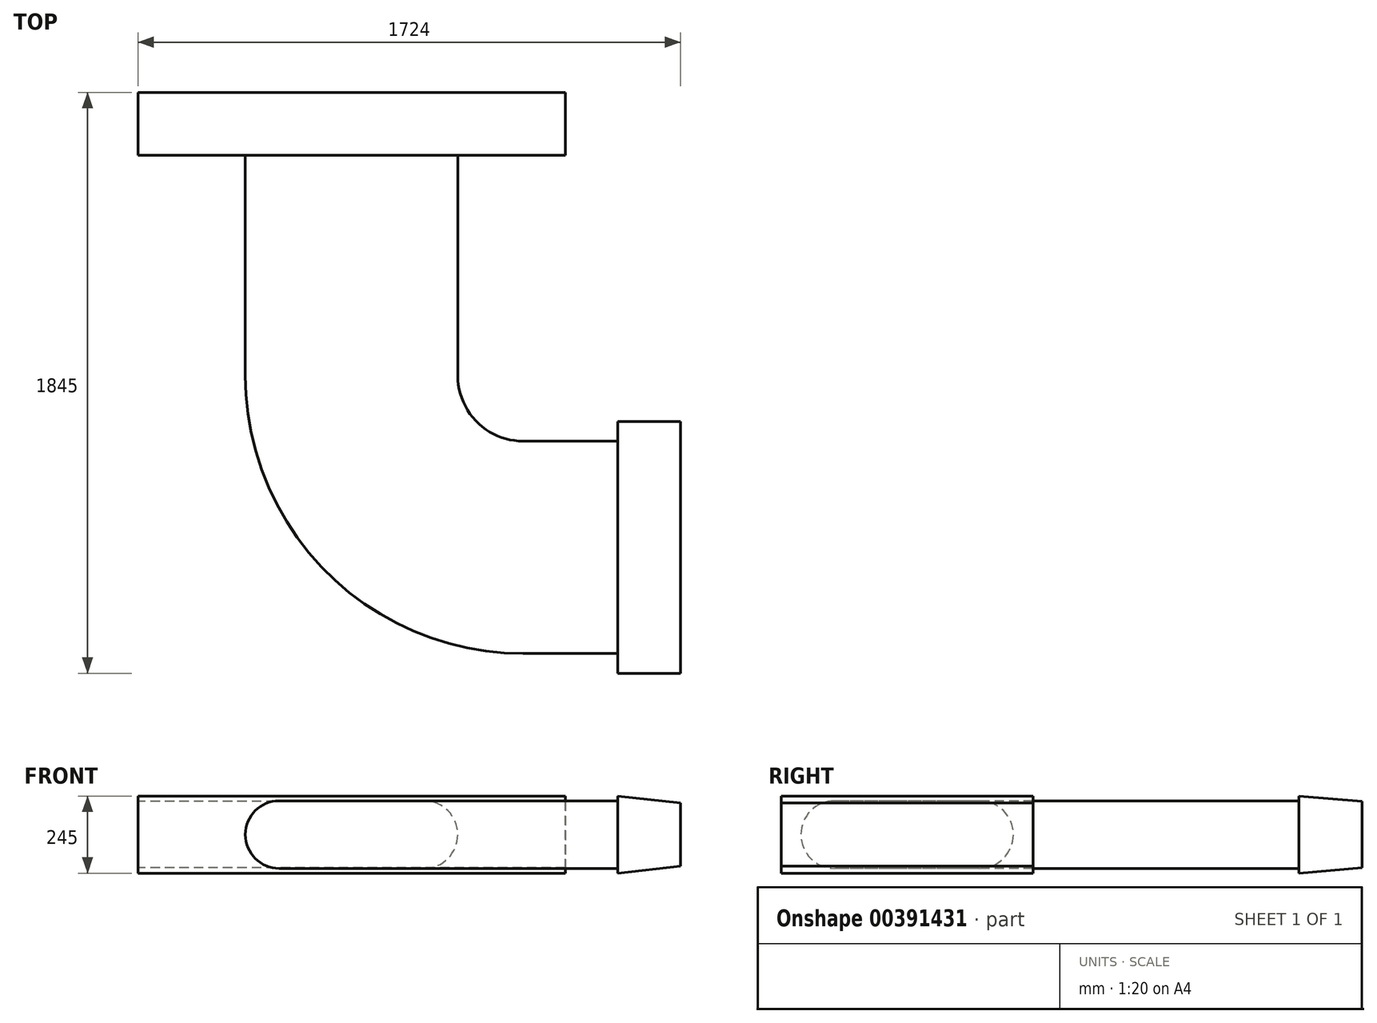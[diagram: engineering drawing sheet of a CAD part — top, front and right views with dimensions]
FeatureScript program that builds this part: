
annotation { "Feature Type Name" : "Feature", "Feature Type Description" : "" }
export const myFeature = defineFeature(function(context is Context, id is Id, definition is map)
    precondition{}
    {
        {
            var Q0;
            Q0=qCreatedBy(makeId("Right.planeOp"),FACE);
            var sketch = newSketch(context, id + "F0", { "sketchPlane" : qUnion([Q0])});
            skLineSegment(sketch, "E0", {"start": v(0, 0) * mm, "end": v(0, 105) * mm});
            skLineSegment(sketch, "E1", {"start": v(0, 0) * mm, "end": v(0, -105) * mm});
            skLineSegment(sketch, "E2", {"start": v(0, 105) * mm, "end": v(-200, 105) * mm, "construction": true});
            skLineSegment(sketch, "E3", {"start": v(0, -105) * mm, "end": v(-200, -105) * mm, "construction": true});
            skLineSegment(sketch, "E4", {"start": v(-200, 105) * mm, "end": v(-200, 122.5) * mm, "construction": true});
            skLineSegment(sketch, "E5", {"start": v(-200, -105) * mm, "end": v(-200, -122.5) * mm, "construction": true});
            skLineSegment(sketch, "E6", {"start": v(-200, 122.5) * mm, "end": v(0, 105) * mm});
            skLineSegment(sketch, "E7", {"start": v(0, -105) * mm, "end": v(-200, -122.5) * mm});
            skLineSegment(sketch, "E8", {"start": v(-200, -122.5) * mm, "end": v(-200, 122.5) * mm});
            skSolve(sketch);
        }
        {
            var Q0;
            Q0=makeQuery(id+"F0.imprint","IMPRINT",FACE,{"disambiguationData":[TD([[makeQuery(id+"F0.imprint","IMPRINT",EDGE,{"derivedFrom":sQuery(id+"F0.wireOp",EDGE,"E0")}),1.0]])]});
            extrude(context, id + "F1", {"entities" : qUnion([Q0]), "depth" : 679 * mm, "hasSecondDirection" : true, "secondDirectionOppositeDirection" : true, "secondDirectionDepth" : 679 * mm});
        }
        {
            var Q0;
            Q0=makeQuery(id+"F1.opExtrude","SWEPT_FACE",FACE,{"disambiguationData":[OSD([sQuery(id+"F0.wireOp",EDGE,"E8")])]});
            var sketch = newSketch(context, id + "F2", { "sketchPlane" : qUnion([Q0])});
            skPoint(sketch, "E9.0", {"position": v(0, 0) * mm});
            skLineSegment(sketch, "E10.bottom", {"start": v(230, -107.5) * mm, "end": v(-230, -107.5) * mm});
            skLineSegment(sketch, "E10.top", {"start": v(230, 107.5) * mm, "end": v(-230, 107.5) * mm});
            skArc(sketch, "E11", {"start": v(-230, 107.5) * mm, "mid": v(-337.5, 0) * mm, "end": v(-230, -107.5) * mm});
            skArc(sketch, "E12", {"start": v(230, -107.5) * mm, "mid": v(337.5, 0) * mm, "end": v(230, 107.5) * mm});
            skSolve(sketch);
        }
        {
            var Q0;
            Q0=makeQuery(id+"F2.imprint","IMPRINT",FACE,{"disambiguationData":[TD([[makeQuery(id+"F2.imprint","IMPRINT",EDGE,{"derivedFrom":sQuery(id+"F2.wireOp",EDGE,"E10.bottom")}),-1.0]])]});
            extrude(context, id + "F3", {"entities" : qUnion([Q0]), "operationType" : NewBodyOperationType.ADD, "depth" : 700 * mm});
        }
        {
            var Q0;
            Q0=makeQuery(id+"F3.opExtrude","CAP_FACE",FACE,{"disambiguationData":[OSD([sQuery(id+"F2.wireOp",EDGE,"E10.bottom"),sQuery(id+"F2.wireOp",EDGE,"E10.top"),sQuery(id+"F2.wireOp",EDGE,"E11"),sQuery(id+"F2.wireOp",EDGE,"E12")])],"isStart":false});
            var sketch = newSketch(context, id + "F4", { "sketchPlane" : qUnion([Q0])});
            skLineSegment(sketch, "E13", {"start": v(0, 107.5) * mm, "end": v(0, -107.5) * mm, "construction": true});
            skLineSegment(sketch, "E14", {"start": v(337.5, 0) * mm, "end": v(-337.5, 0) * mm, "construction": true});
            skPoint(sketch, "E15", {"position": v(0, 0) * mm});
            skSolve(sketch);
        }
        {
            var Q0;
            Q0=sQuery(id+"F4.wireOp",EDGE,"E14");
            cPlane(context, id + "F5", {"entities" : qUnion([Q0]), "cplaneType" : CPlaneType.LINE_ANGLE, "offset" : 25 * mm, "angle" : 90 * degree, "width" : 150 * mm, "height" : 150 * mm});
        }
        {
            var Q0;
            Q0=qCreatedBy(id+"F5.planeOp",FACE);
            var sketch = newSketch(context, id + "F6", { "sketchPlane" : qUnion([Q0])});
            skPoint(sketch, "E16.0", {"position": v(0, -900) * mm});
            skLineSegment(sketch, "E17", {"start": v(0, -900) * mm, "end": v(545, -900) * mm, "construction": true});
            skLineSegment(sketch, "E18", {"start": v(545, -900) * mm, "end": v(545, -1445) * mm, "construction": true});
            skArc(sketch, "E19", {"start": v(0, -900) * mm, "mid": v(159.63, -1285.37) * mm, "end": v(545, -1445) * mm});
            skSolve(sketch);
        }
        {
            var Q0;
            Q0=makeQuery(id+"F4.imprint","IMPRINT",FACE,{"disambiguationData":[TD([[makeQuery(id+"F4.imprint","IMPRINT",EDGE,{"derivedFrom":makeQuery(id+"F3.opExtrude","CAP_EDGE",EDGE,{"disambiguationData":[OSD([sQuery(id+"F2.wireOp",EDGE,"E10.bottom")])],"isStart":false})}),-1.0]])]});
            var Q1;
            Q1=sQuery(id+"F6.wireOp",EDGE,"E19");
            sweep(context, id + "F7", {"operationType" : NewBodyOperationType.ADD, "profiles" : qUnion([Q0]), "path" : qUnion([Q1])});
        }
        {
            var Q0;
            Q0=makeQuery(id+"F7.opSweep","CAP_FACE",FACE,{"disambiguationData":[OSD([sQuery(id+"F2.wireOp",EDGE,"E10.bottom"),sQuery(id+"F2.wireOp",EDGE,"E10.top"),sQuery(id+"F2.wireOp",EDGE,"E11"),sQuery(id+"F2.wireOp",EDGE,"E12"),sQuery(id+"F6.wireOp",VERTEX,"E19.end")])],"isStart":false});
            extrude(context, id + "F8", {"entities" : qUnion([Q0]), "operationType" : NewBodyOperationType.ADD, "depth" : 300 * mm});
        }
        {
            var Q0;
            Q0=makeQuery(id+"F8.opExtrude","CAP_FACE",FACE,{"disambiguationData":[OSD([sQuery(id+"F2.wireOp",EDGE,"E10.bottom"),sQuery(id+"F2.wireOp",EDGE,"E10.top"),sQuery(id+"F2.wireOp",EDGE,"E11"),sQuery(id+"F2.wireOp",EDGE,"E12"),sQuery(id+"F6.wireOp",VERTEX,"E19.end")])],"isStart":false});
            var sketch = newSketch(context, id + "F9", { "sketchPlane" : qUnion([Q0])});
            skLineSegment(sketch, "E20", {"start": v(-1445, 107.5) * mm, "end": v(-1445, -107.5) * mm, "construction": true});
            skLineSegment(sketch, "E21", {"start": v(-1782.5, 0) * mm, "end": v(-1107.5, 0) * mm, "construction": true});
            skPoint(sketch, "E22", {"position": v(-1445, 0) * mm});
            skSolve(sketch);
        }
        {
            var Q0;
            Q0=sQuery(id+"F9.wireOp",EDGE,"E20");
            cPlane(context, id + "F10", {"entities" : qUnion([Q0]), "cplaneType" : CPlaneType.LINE_ANGLE, "offset" : 25 * mm, "angle" : 90 * degree, "width" : 150 * mm, "height" : 150 * mm});
        }
        {
            var Q0;
            Q0=qCreatedBy(id+"F10.planeOp",FACE);
            var sketch = newSketch(context, id + "F11", { "sketchPlane" : qUnion([Q0])});
            skPoint(sketch, "E23.0", {"position": v(-845, 0) * mm});
            skLineSegment(sketch, "E24", {"start": v(-845, 0) * mm, "end": v(-845, 122.5) * mm});
            skLineSegment(sketch, "E25", {"start": v(-845, 0) * mm, "end": v(-845, -122.5) * mm});
            skLineSegment(sketch, "E26", {"start": v(-845, 0) * mm, "end": v(-1045, 0) * mm, "construction": true});
            skLineSegment(sketch, "E27", {"start": v(-1045, 0) * mm, "end": v(-1045, 100) * mm});
            skLineSegment(sketch, "E28", {"start": v(-1045, 0) * mm, "end": v(-1045, -100) * mm});
            skLineSegment(sketch, "E29", {"start": v(-1045, 100) * mm, "end": v(-845, 122.5) * mm});
            skLineSegment(sketch, "E30", {"start": v(-1045, -100) * mm, "end": v(-845, -122.5) * mm});
            skSolve(sketch);
        }
        {
            var Q0;
            Q0=makeQuery(id+"F11.imprint","IMPRINT",FACE,{"disambiguationData":[TD([[makeQuery(id+"F11.imprint","IMPRINT",EDGE,{"derivedFrom":sQuery(id+"F11.wireOp",EDGE,"E24")}),1.0]])]});
            extrude(context, id + "F12", {"entities" : qUnion([Q0]), "operationType" : NewBodyOperationType.ADD, "depth" : 400 * mm, "hasSecondDirection" : true, "secondDirectionOppositeDirection" : true, "secondDirectionDepth" : 400 * mm});
        }
    });
